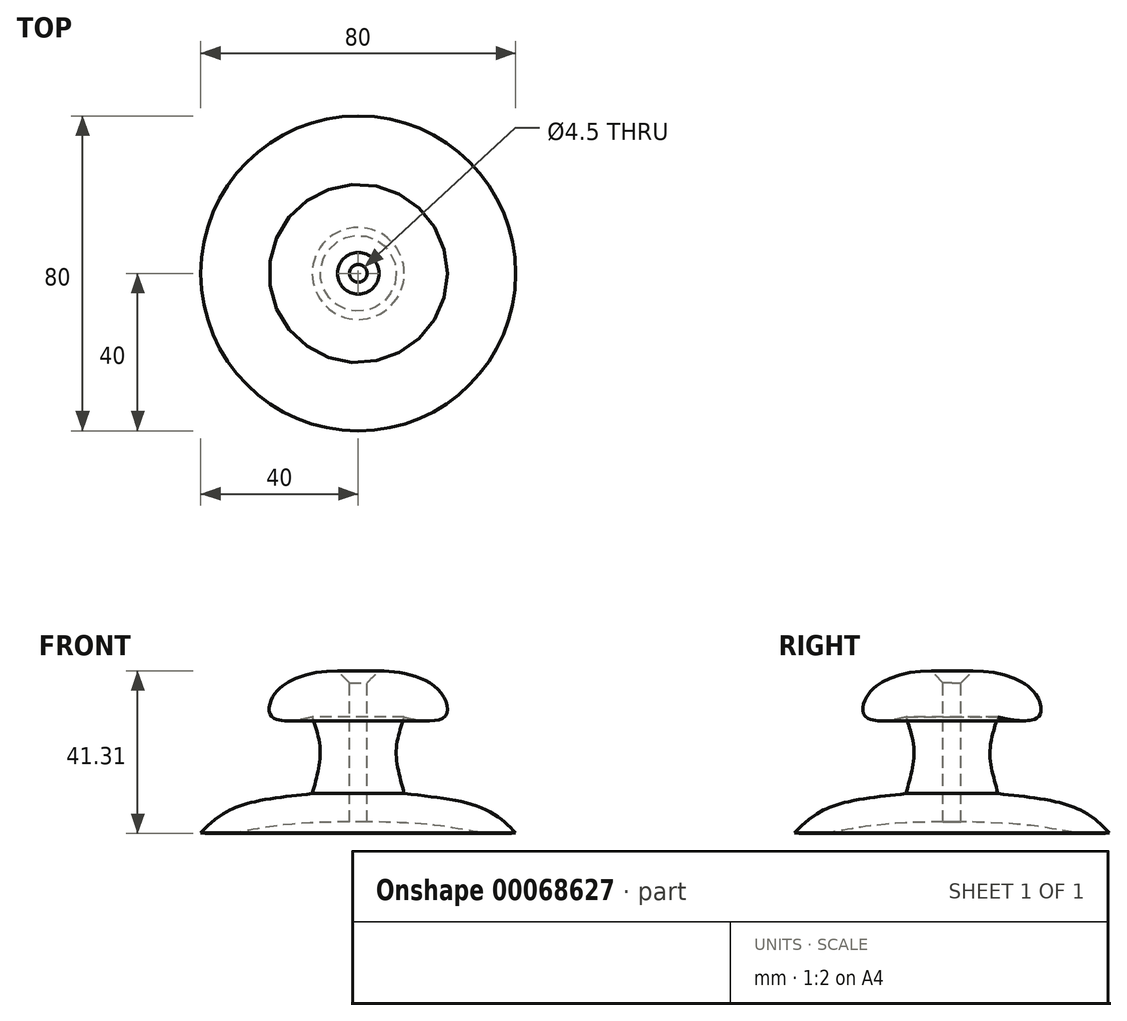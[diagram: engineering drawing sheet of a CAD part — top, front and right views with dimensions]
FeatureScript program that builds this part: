
annotation { "Feature Type Name" : "Feature", "Feature Type Description" : "" }
export const myFeature = defineFeature(function(context is Context, id is Id, definition is map)
    precondition{}
    {
        {
            var Q0;
            Q0=qCreatedBy(makeId("Front.planeOp"),FACE);
            var sketch = newSketch(context, id + "F0", { "sketchPlane" : qUnion([Q0])});
            skLineSegment(sketch, "E0.rect.bottom", {"start": v(40, 10) * mm, "end": v(-40, 10) * mm});
            skLineSegment(sketch, "E0.rect.top", {"start": v(40, -10) * mm, "end": v(-40, -10) * mm});
            skLineSegment(sketch, "E0.rect.left", {"start": v(40, 10) * mm, "end": v(40, -10) * mm});
            skLineSegment(sketch, "E0.rect.right", {"start": v(-40, 10) * mm, "end": v(-40, -10) * mm});
            skFitSpline(sketch, "E1", {"points": [v(40, 0) * mm, v(31.83, 6.17) * mm, v(11.68, 10) * mm], "startDerivative": vector(-13.76, 15.11) * mm, "endDerivative": vector(-40.27, 4.77) * mm});
            skFitSpline(sketch, "E2", {"points": [v(11.68, 10) * mm, v(9.65, 20.54) * mm, v(11.68, 29.44) * mm], "startDerivative": vector(-5.38, 20.43) * mm, "endDerivative": vector(5.65, 16.18) * mm});
            skFitSpline(sketch, "E3", {"points": [v(11.68, 29.44) * mm, v(21.86, 29.44) * mm, v(20.67, 35.99) * mm, v(9.13, 40.93) * mm, v(0, 41.05) * mm], "startDerivative": vector(34.7, -9.34) * mm, "endDerivative": vector(-27.56, 0.02) * mm});
            skPoint(sketch, "E4.3.internal.snap0", {"position": v(0, 10) * mm});
            skFitSpline(sketch, "E4", {"points": [v(40, 0) * mm, v(32.27, 0) * mm, v(19.63, 1.91) * mm, v(0, 2.74) * mm], "startDerivative": vector(-30.04, -1.69) * mm, "endDerivative": vector(-34.15, -0.58) * mm});
            skLineSegment(sketch, "E5", {"start": v(0, 41.05) * mm, "end": v(0, 2.74) * mm});
            skLineSegment(sketch, "E6.left", {"start": v(0, 0) * mm, "end": v(0, 10) * mm});
            skLineSegment(sketch, "E7.left", {"start": v(0, 2.74) * mm, "end": v(0, 10) * mm});
            skLineSegment(sketch, "E7.right", {"start": v(2.25, 2.74) * mm, "end": v(2.25, 41.1) * mm});
            skLineSegment(sketch, "E8.trimOffspring", {"start": v(0, 41.05) * mm, "end": v(0, 41.1) * mm});
            skSolve(sketch);
        }
        {
            var Q0;
            {var subQ0=sQuery(id+"F0.wireOp",EDGE,"E2");Q0=makeQuery(id+"F0.imprint","IMPRINT",FACE,{"disambiguationData":[TD([[makeQuery(id+"F0.imprint","IMPRINT",EDGE,{"derivedFrom":subQ0}),1.0]])]});}
            var Q1;
            {var subQ0=sQuery(id+"F0.wireOp",EDGE,"E1");Q1=makeQuery(id+"F0.imprint","IMPRINT",FACE,{"disambiguationData":[TD([[makeQuery(id+"F0.imprint","IMPRINT",EDGE,{"derivedFrom":subQ0}),1.0]])]});}
            var Q2;
            Q2=sQuery(id+"F0.wireOp",EDGE,"E5");
            revolve(context, id + "F1", {"entities" : qUnion([Q0, Q1]), "axis" : qUnion([Q2]), "revolveType" : RevolveType.FULL});
        }
        {
            var Q0;
            Q0=makeQuery(id+"F1.opRevolve","SWEPT_EDGE",EDGE,{"disambiguationData":[OSD([sQuery(id+"F0.wireOp",EDGE,"E3"),sQuery(id+"F0.wireOp",EDGE,"E7.right")])]});
            chamfer(context, id + "F2", {"entities" : qUnion([Q0]), "width" : 3 * mm, "tangentPropagation" : true});
        }
    });
